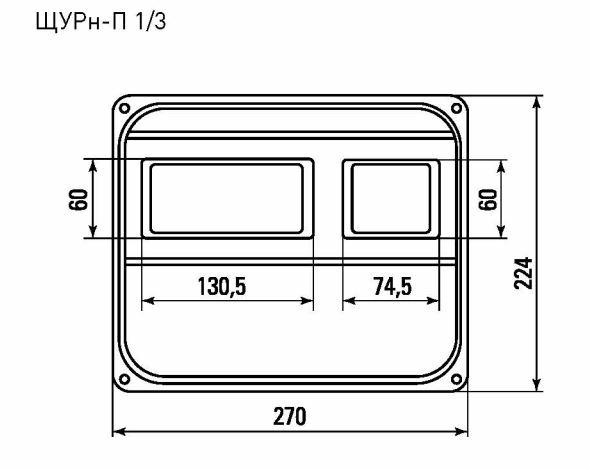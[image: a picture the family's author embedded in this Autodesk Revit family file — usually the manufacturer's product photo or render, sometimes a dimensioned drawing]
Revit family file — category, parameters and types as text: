
# Revit family: EKF_EE_ЩМПг_Гранит_IP66_У1_EKF_PROxima
name_source: partatom
category: Электрооборудование
units: mm (PartAtom-declared; Revit-internal decimal feet)

## family parameters
Всегда вертикально = Да
На основе рабочей плоскости = Нет
Общий = Нет
При загрузке вырезать с полостями = Нет
Размер круглого соединителя = Использовать диаметр
Тип детали = Силовой щит
Точка расчета площади = Да

## types (7) — shared parameters
ADSK_Единица измерения = компл.
ADSK_Завод-изготовитель = EKF
ADSK_Количество = 1
ADSK_Материал = RAL 7035_Сталь
Изготовитель = EKF
Серия номенклатуры = PROxima
Степень защиты IP = IP66
ТВ = EKF
Тип установки = Навесной
zero-valued in all types: ADSK_Масса, Количество DIN-реек, Количество модулей на DIN-рейке, Максимальное количество модулей

## per-type parameters (varying)
| type | ADSK_Код изделия | ADSK_Марка | ADSK_Наименование | ADSK_Обозначение | ADSK_Размер_Высота | ADSK_Размер_Глубина | ADSK_Размер_Ширина | Описание | Тип |
| ЩМПг - 40.31.22 "Гранит" IP66 У1 EKF PROxima | mb65-1 | ЩМПг - 40.31.22 IP66 У1 | Щит с монтажной панелью ЩМПг - 40.31.22 Гранит IP66 У1 EKF PROxima | ЩМПг - 40.31.22 IP66 У1 | 400 мм | 220 мм | 310 мм | Щит с монтажной панелью ЩМПг - 40.31.22 Гранит IP66 У1 EKF PROxima | 113 мм |
| ЩМПг - 50.40.22 "Гранит" IP66 У1 EKF PROxima | mb65-2 | ЩМПг - 50.40.22 IP66 У1 | Щит с монтажной панелью ЩМПг - 50.40.22 Гранит IP66 У1 EKF PROxima | ЩМПг - 50.40.22 IP66 У1 | 500 мм | 220 мм | 400 мм | Щит с монтажной панелью ЩМПг - 50.40.22 Гранит IP66 У1 EKF PROxima | 114 мм |
| ЩМПг - 65.50.22 "Гранит" IP66 У1 EKF PROxima | mb65-3 | ЩМПг - 65.50.22 IP66 У1 | Щит с монтажной панелью ЩМПг - 65.50.22 Гранит IP66 У1 EKF PROxima | ЩМПг - 65.50.22 IP66 У1 | 650 мм | 220 мм | 500 мм | Щит с монтажной панелью ЩМПг - 65.50.22 Гранит IP66 У1 EKF PROxima | 115 мм |
| ЩМПг - 80.60.25 "Гранит" IP66 У1 EKF PROxima | mb65-4 | ЩМПг - 80.60.25 IP66 У1 | Щит с монтажной панелью ЩМПг - 80.60.25 Гранит IP66 У1 EKF PROxima | ЩМПг - 80.60.25 IP66 У1 | 800 мм | 250 мм | 600 мм | Щит с монтажной панелью ЩМПг - 80.60.25 Гранит IP66 У1 EKF PROxima | 116 мм |
| ЩМПг-100.65.27 "Гранит" IP66 У1 EKF PROxima | mb65-5 | ЩМПг-100.65.27 IP66 У1 | Щит с монтажной панелью ЩМПг-100.65.27 Гранит IP66 У1 EKF PROxima | ЩМПг-100.65.27 IP66 У1 | 1000 мм | 270 мм | 650 мм | Щит с монтажной панелью ЩМПг-100.65.27 Гранит IP66 У1 EKF PROxima | 117 мм |
| ЩМПг-120.65.27 "Гранит" IP66 У1 EKF PROxima | mb65-6 | ЩМПг-120.65.27 IP66 У1 | Щит с монтажной панелью ЩМПг-120.65.27 Гранит IP66 У1 EKF PROxima | ЩМПг-120.65.27 IP66 У1 | 1200 мм | 270 мм | 650 мм | Щит с монтажной панелью ЩМПг-120.65.27 Гранит IP66 У1 EKF PROxima | 118 мм |
| ЩМПг-140.65.27 "Гранит" IP66 У1 EKF PROxima | mb65-7 | ЩМПг-140.65.27 IP66 У1 | Щит с монтажной панелью ЩМПг-140.65.27 Гранит IP66 У1 EKF PROxima | ЩМПг-140.65.27 IP66 У1 | 1400 мм | 270 мм | 650 мм | Щит с монтажной панелью ЩМПг-140.65.27 Гранит IP66 У1 EKF PROxima | 119 мм |
